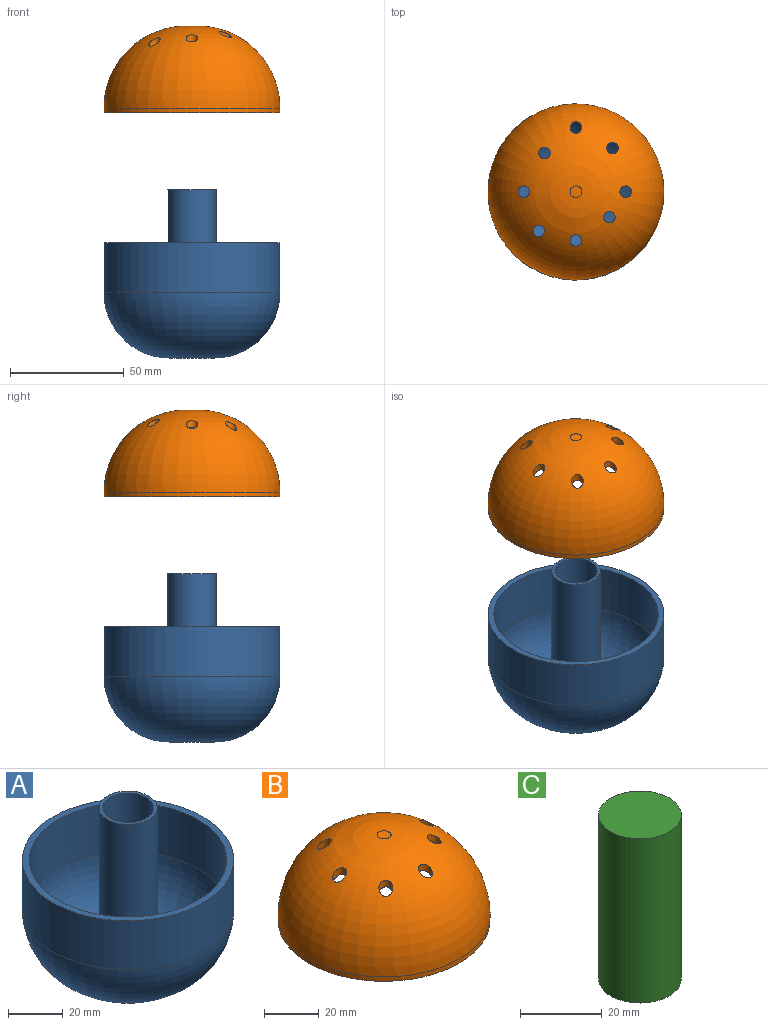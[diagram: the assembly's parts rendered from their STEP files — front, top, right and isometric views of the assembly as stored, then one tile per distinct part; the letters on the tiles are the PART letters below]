
ASSEMBLY  parts=3 mates=4
PART A: 11 faces, bbox 77.5x77.5x74.2 mm
  f0: torus R=9.91mm, axis (0,0,1), area 6864.6mm2, adj f5,f6
  f1: cylinder r=38.73mm len=77.47mm, axis (0,0,-1), area 5349.3mm2, adj f2,f4
  f2: plane 77.47x77.47mm, normal (0,0,1), area 597.9mm2, adj f1,f5
  f3: plane 19.83x19.83mm, normal (0,0,-1), area 308.8mm2, adj f4
  f4: torus R=9.91mm, axis (0,0,1), area 8039.2mm2, adj f1,f3
  f5: cylinder r=36.2mm len=72.39mm, axis (0,0,-1), area 4998.5mm2, adj f0,f2
  f6: cylinder r=10.64mm len=71.62mm, axis (0,0,-1), area 4786.2mm2, adj f0,f7
  f7: plane 21.27x21.27mm, normal (0,0,1), area 79.8mm2, adj f6,f10
  f8: torus R=9.91mm, axis (0,0,1), area 33.2mm2, adj f9,f10
  f9: plane 19.83x19.83mm, normal (0,0,1), area 308.8mm2, adj f8
  f10: cylinder r=9.37mm len=72.89mm, axis (0,0,-1), area 4289.7mm2, adj f7,f8
PART B: 15 faces, bbox 77.5x77.5x38.1 mm
  f0: torus R=2.56mm, axis (0,0,1), area 8937.2mm2, adj f2,f3,f7,f8,f9,f10,f11,f12
  f1: torus R=2.56mm, axis (0,0,1), area 7750.3mm2, adj f5,f6,f7,f8,f9,f10,f11,f12
  f2: cylinder r=38.73mm len=77.47mm, axis (0,0,-1), area 467.4mm2, adj f0,f4
  f3: plane 5.11x5.11mm, normal (0,0,1), area 20.5mm2, adj f0
  f4: plane 77.47x77.47mm, normal (0,0,-1), area 597.9mm2, adj f2,f5
  f5: cylinder r=36.2mm len=72.39mm, axis (0,0,-1), area 436.8mm2, adj f1,f4
  f6: plane 5.11x5.11mm, normal (0,0,-1), area 20.5mm2, adj f1
  f7: cylinder r=2.54mm len=6.34mm, axis (0,0,-1), area 48.5mm2, adj f0,f1
  f8: cylinder r=2.54mm len=7.17mm, axis (0,0,-1), area 51.5mm2, adj f0,f1
  f9: cylinder r=2.54mm len=5.49mm, axis (0,0,-1), area 45.8mm2, adj f0,f1
  f10: cylinder r=2.54mm len=7.71mm, axis (0,0,-1), area 53.6mm2, adj f0,f1
  f11: cylinder r=2.54mm len=6.5mm, axis (0,0,-1), area 49mm2, adj f0,f1
  f12: cylinder r=2.54mm len=6.86mm, axis (0,0,-1), area 50.3mm2, adj f0,f1
  f13: cylinder r=2.54mm len=9.49mm, axis (0,0,-1), area 60.8mm2, adj f0,f1
  f14: cylinder r=2.54mm len=6.5mm, axis (0,0,-1), area 49mm2, adj f0,f1
PART C: 5 faces, bbox 20.3x20.3x49.3 mm
  f0: cylinder r=10.16mm len=49.28mm, axis (0,0,-1), area 3145.6mm2, adj f1,f2
  f1: plane 20.32x20.32mm, normal (0,0,1), area 324.3mm2, adj f0
  f2: plane 20.32x20.32mm, normal (0,0,-1), area 76.6mm2, adj f0,f3
  f3: cylinder r=8.88mm len=25.4mm, axis (0,0,-1), area 1417.1mm2, adj f2,f4
  f4: plane 17.76x17.76mm, normal (0,0,-1), area 247.7mm2, adj f3
PLACE A t=(52.51,-91.7,-132.87)mm
PLACE B t=(52.51,-91.7,-24.82)mm
PLACE C rot(axis=(1,0,0),180deg) t=(52.51,-91.7,-82.32)mm
MATE slider C.f0 <-> A.f0  axis (0,0,-1) through (52.51,-91.7,-131.6)mm
MATE slider B.f0 <-> A.f0  axis (0,0,1) through (52.51,-91.7,13.28)mm
MATE parallel A.f0 <-> B.f0  axis (0,0,1) through (52.51,-91.7,-82.07)mm
MATE slider A.f0 <-> B.f0  axis (0,0,1) through (52.51,-91.7,-82.07)mm
